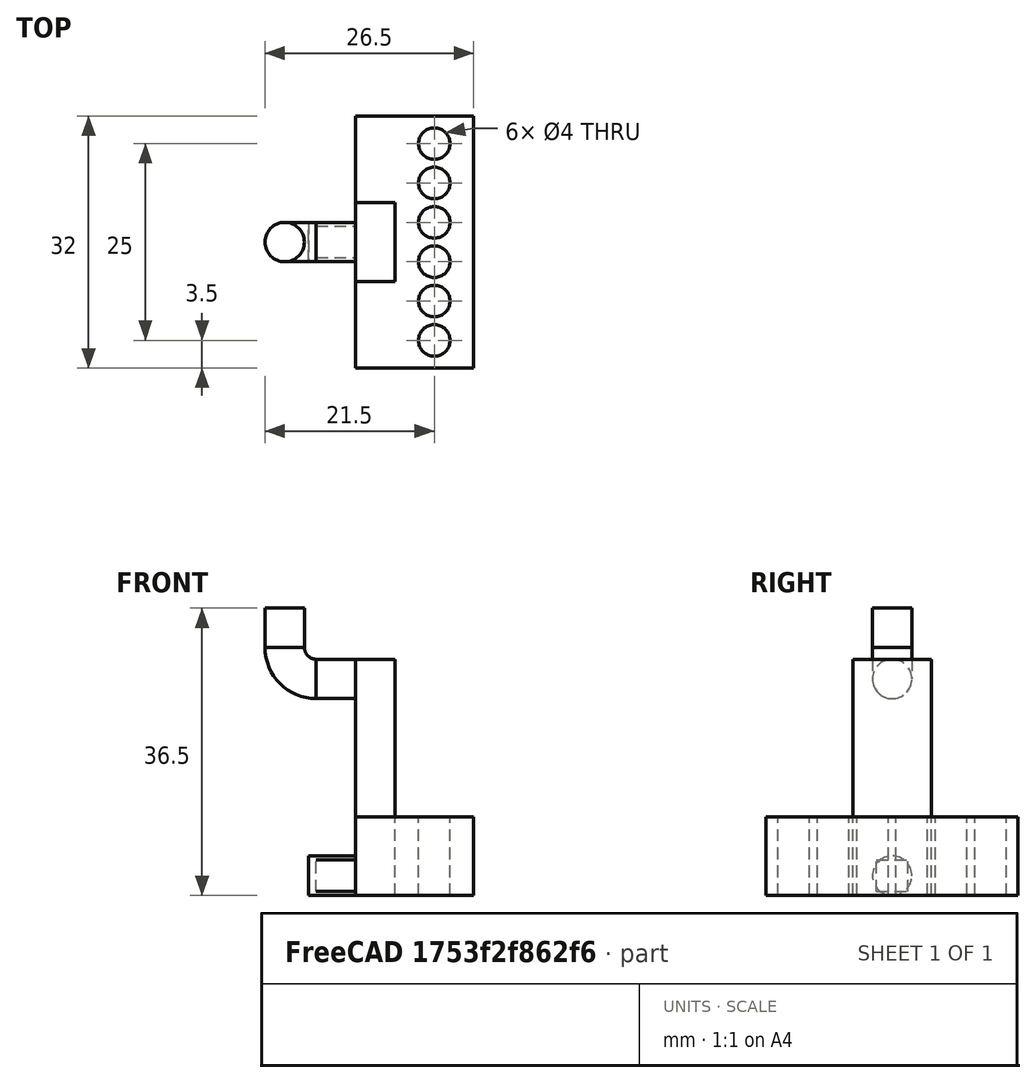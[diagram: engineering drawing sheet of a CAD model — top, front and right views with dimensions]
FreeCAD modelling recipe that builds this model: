
FCSTD DOCUMENT  (FreeCAD 0.17R13522 (Git))
Label: hexholder
License: All rights reserved
LicenseURL: http://en.wikipedia.org/wiki/All_rights_reserved
objects: Part::Cylinder×4, Part::Box×3, Part::Torus×1, Part::FeaturePython×1, Part::Cut×1
note: 10 computed .brp shape members not serialized (recipe doc carries the construction recipe); baked Part::Feature solids carry a one-line shape summary decoded from their .brp

FEATURE [Part::Cylinder] Cylinder002
  Angle = 360
  AttacherType = Attacher::AttachEngine3D
  Height = 6
  Placement = pos=(-5,0,2.5) rot=(0,-1,0;1.5708rad)
  Radius = 2.5
FEATURE [Part::Box] Box001  label="Cube001"
  AttacherType = Attacher::AttachEngine3D
  Height = 30
  Length = 5
  Placement = pos=(-5,-5,0) rot=(0,0,1;0rad)
  Width = 10
FEATURE [Part::Cylinder] Cylinder003
  Angle = 360
  AttacherType = Attacher::AttachEngine3D
  Height = 5
  Placement = pos=(-5,0,27.5) rot=(0,-1,0;1.5708rad)
  Radius = 2.5
FEATURE [Part::Torus] Torus
  Angle1 = -180
  Angle2 = 180
  Angle3 = 90
  AttacherType = Attacher::AttachEngine3D
  Placement = pos=(-10,0,31.5) rot=(0.57735,-0.57735,-0.57735;4.18879rad)
  Radius1 = 4
  Radius2 = 2.5
FEATURE [Part::Cylinder] Cylinder004
  Angle = 360
  AttacherType = Attacher::AttachEngine3D
  Height = 5
  Placement = pos=(-14,0,31.5) rot=(0,0,1;0rad)
  Radius = 2.5
FEATURE [Part::Box] Box002  label="Cube002"
  AttacherType = Attacher::AttachEngine3D
  Height = 4
  Length = 5
  Placement = pos=(-10,-2,0.5) rot=(0,0,1;0rad)
  Width = 4
FEATURE [Part::Box] Box  label="Cube"
  AttacherType = Attacher::AttachEngine3D
  Height = 10
  Length = 15
  Placement = pos=(-5,-16,0) rot=(0,0,1;0rad)
  Width = 32
FEATURE [Part::Cylinder] Cylinder
  Angle = 360
  AttacherType = Attacher::AttachEngine3D
  Height = 10
  Placement = pos=(5,-12.5,0) rot=(0,0,1;0rad)
  Radius = 2
FEATURE [Part::FeaturePython] Array  # Draft array (typed FeaturePython)
  Angle = 360
  ArrayType = 0
  Axis = (0,0,1)
  Base = -> Cylinder
  Center = (0,0,0)
  Fuse = false
  IntervalAxis = (0,0,0)
  IntervalX = (1,0,0)
  IntervalY = (0,5,0)
  IntervalZ = (0,0,0)
  NumberPolar = 1
  NumberX = 1
  NumberY = 6
  NumberZ = 1
FEATURE [Part::Cut] Cut
  Base = -> Box
  Tool = -> Array
